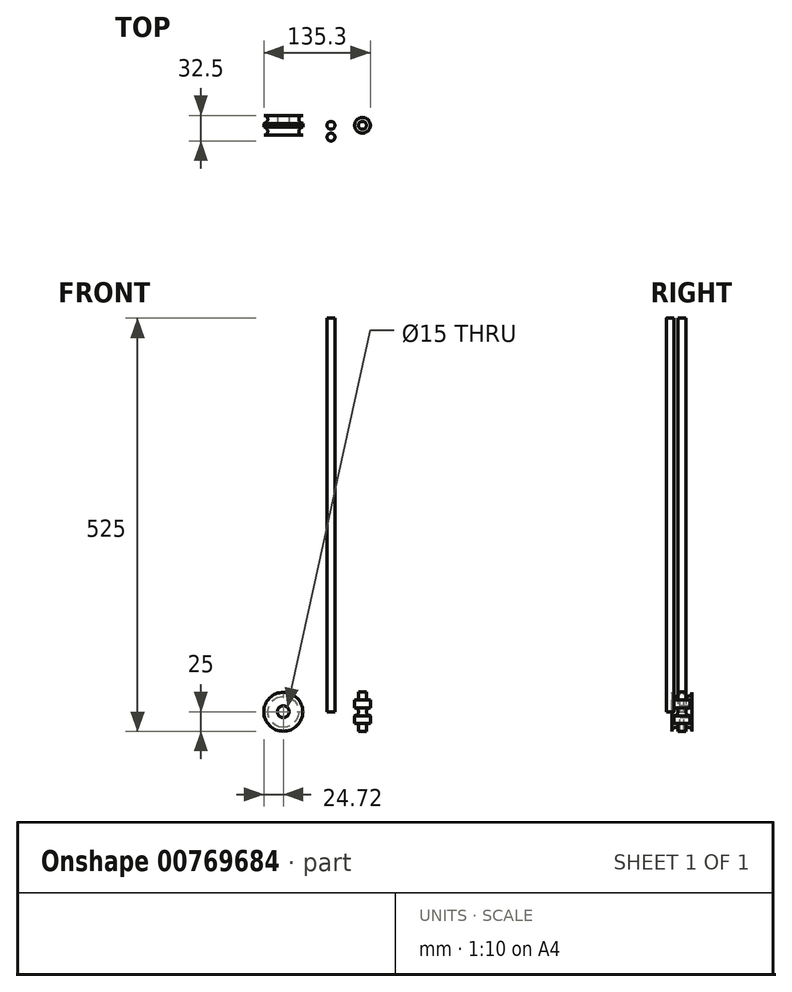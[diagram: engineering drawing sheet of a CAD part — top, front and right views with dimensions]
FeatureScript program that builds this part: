
annotation { "Feature Type Name" : "Feature", "Feature Type Description" : "" }
export const myFeature = defineFeature(function(context is Context, id is Id, definition is map)
    precondition{}
    {
        {
            var Q0;
            Q0=qCreatedBy(makeId("Top.planeOp"),FACE);
            var sketch = newSketch(context, id + "F0", { "sketchPlane" : qUnion([Q0])});
            skCircle(sketch, "E0", {"center": v(0, 0) * mm, "radius": 5 * mm});
            skLineSegment(sketch, "E1", {"start": v(0, 0) * mm, "end": v(0, -15) * mm});
            skCircle(sketch, "E2", {"center": v(0, -15) * mm, "radius": 5 * mm});
            skSolve(sketch);
        }
        {
            var Q0;
            Q0 = qSketchRegion(id + "F0", true);
            extrude(context, id + "F1", {"entities" : qUnion([Q0]), "depth" : 500 * mm, "offsetDistance" : 25 * mm});
        }
        {
            var Q0;
            Q0=qCreatedBy(makeId("Top.planeOp"),FACE);
            var sketch = newSketch(context, id + "F2", { "sketchPlane" : qUnion([Q0])});
            skLineSegment(sketch, "E3", {"start": v(0, 0) * mm, "end": v(40, 0) * mm});
            skCircle(sketch, "E4", {"center": v(40, 0) * mm, "radius": 10 * mm});
            skSolve(sketch);
        }
        {
            var Q0;
            Q0=makeQuery(id+"F2.imprint","IMPRINT",FACE,{"disambiguationData":[TD([[makeQuery(id+"F2.imprint","IMPRINT",EDGE,{"derivedFrom":sQuery(id+"F2.wireOp",EDGE,"E4")}),1.0]])]});
            extrude(context, id + "F3", {"entities" : qUnion([Q0]), "depth" : 50 * mm, "offsetDistance" : 25 * mm, "symmetric" : true});
        }
        {
            var Q0;
            Q0=qCreatedBy(makeId("Right.planeOp"),FACE);
            cPlane(context, id + "F4", {"entities" : qUnion([Q0]), "cplaneType" : CPlaneType.OFFSET, "offset" : 40 * mm, "width" : 150 * mm, "height" : 150 * mm});
        }
        {
            var Q0;
            Q0=qCreatedBy(id+"F4.planeOp",FACE);
            var sketch = newSketch(context, id + "F5", { "sketchPlane" : qUnion([Q0])});
            skLineSegment(sketch, "E5", {"start": v(0, 0) * mm, "end": v(10, 0) * mm});
            skCircle(sketch, "E6", {"center": v(10, 0) * mm, "radius": 5 * mm});
            skLineSegment(sketch, "E7", {"start": v(0, 0) * mm, "end": v(0, 15.21) * mm});
            skSolve(sketch);
        }
        {
            var Q0;
            Q0=makeQuery(id+"F5.imprint","IMPRINT",FACE,{"disambiguationData":[TD([[makeQuery(id+"F5.imprint","IMPRINT",EDGE,{"derivedFrom":sQuery(id+"F5.wireOp",EDGE,"E6")}),1.0]])]});
            var Q1;
            Q1=makeQuery(id+"F3.opExtrude","SWEPT_FACE",FACE,{"disambiguationData":[OSD([sQuery(id+"F2.wireOp",EDGE,"E4")])]});
            revolve(context, id + "F6", {"operationType" : NewBodyOperationType.REMOVE, "surfaceOperationType" : NewSurfaceOperationType.NEW, "entities" : qUnion([Q0]), "axis" : qUnion([Q1]), "revolveType" : RevolveType.FULL, "oppositeDirection" : true});
        }
        {
            var Q0;
            Q0=makeQuery(id+"F3.opExtrude","CAP_FACE",FACE,{"disambiguationData":[OSD([sQuery(id+"F2.wireOp",EDGE,"E4")])],"isStart":false});
            var sketch = newSketch(context, id + "F7", { "sketchPlane" : qUnion([Q0])});
            skCircle(sketch, "E8", {"center": v(40, 0) * mm, "radius": 5 * mm});
            skCircle(sketch, "E9", {"center": v(40, 0) * mm, "radius": 10 * mm});
            skSolve(sketch);
        }
        {
            var Q0;
            Q0 = qSketchRegion(id + "F7", true);
            extrude(context, id + "F8", {"entities" : qUnion([Q0]), "operationType" : NewBodyOperationType.REMOVE, "oppositeDirection" : true, "depth" : 10 * mm, "offsetDistance" : 25 * mm});
        }
        {
            var Q0;
            Q0=makeQuery(id+"F3.opExtrude","CAP_FACE",FACE,{"disambiguationData":[OSD([sQuery(id+"F2.wireOp",EDGE,"E4")])],"isStart":true});
            var sketch = newSketch(context, id + "F9", { "sketchPlane" : qUnion([Q0])});
            skCircle(sketch, "E10", {"center": v(40, 0) * mm, "radius": 5 * mm});
            skCircle(sketch, "E11", {"center": v(40, 0) * mm, "radius": 10 * mm});
            skSolve(sketch);
        }
        {
            var Q0;
            Q0 = qSketchRegion(id + "F9", true);
            extrude(context, id + "F10", {"entities" : qUnion([Q0]), "operationType" : NewBodyOperationType.REMOVE, "oppositeDirection" : true, "depth" : 10 * mm, "offsetDistance" : 25 * mm});
        }
        {
            var Q0;
            Q0=qCreatedBy(makeId("Top.planeOp"),FACE);
            var sketch = newSketch(context, id + "F11", { "sketchPlane" : qUnion([Q0])});
            skLineSegment(sketch, "E12", {"start": v(0, 0) * mm, "end": v(-35.86, 0) * mm});
            skLineSegment(sketch, "E13", {"start": v(-35.86, 0) * mm, "end": v(-35.86, -7.5) * mm});
            skLineSegment(sketch, "E14", {"start": v(-35.86, 0) * mm, "end": v(-35.86, 7.5) * mm});
            skCircle(sketch, "E15", {"center": v(-35.86, 7.5) * mm, "radius": 5 * mm});
            skCircle(sketch, "E16", {"center": v(-35.86, -7.5) * mm, "radius": 5 * mm});
            skLineSegment(sketch, "E17", {"start": v(-35.86, 12.5) * mm, "end": v(-60.58, 12.5) * mm});
            skLineSegment(sketch, "E18", {"start": v(-35.86, -12.5) * mm, "end": v(-60.58, -12.5) * mm});
            skLineSegment(sketch, "E19", {"start": v(-60.58, -12.5) * mm, "end": v(-60.58, 12.5) * mm});
            skLineSegment(sketch, "E20", {"start": v(-35.86, 12.5) * mm, "end": v(-35.86, 7.5) * mm});
            skLineSegment(sketch, "E21", {"start": v(-35.86, -7.5) * mm, "end": v(-35.86, -12.5) * mm});
            skSolve(sketch);
        }
        {
            var Q0;
            {var subQ4=sQuery(id+"F11.wireOp",EDGE,"E17");Q0=makeQuery(id+"F11.imprint","IMPRINT",FACE,{"disambiguationData":[TD([[makeQuery(id+"F11.imprint","IMPRINT",EDGE,{"derivedFrom":subQ4}),1.0]])]});}
            var Q1;
            Q1=sQuery(id+"F11.wireOp",EDGE,"E19");
            revolve(context, id + "F12", {"surfaceOperationType" : NewSurfaceOperationType.NEW, "entities" : qUnion([Q0]), "axis" : qUnion([Q1]), "revolveType" : RevolveType.FULL});
        }
        {
            var Q0;
            Q0=makeQuery(id+"F12.opRevolve","SWEPT_FACE",FACE,{"disambiguationData":[OSD([sQuery(id+"F11.wireOp",EDGE,"E18")])]});
            var sketch = newSketch(context, id + "F13", { "sketchPlane" : qUnion([Q0])});
            skCircle(sketch, "E22", {"center": v(-60.58, 0) * mm, "radius": 7.5 * mm});
            skSolve(sketch);
        }
        {
            var Q0;
            Q0 = qSketchRegion(id + "F13", true);
            extrude(context, id + "F14", {"entities" : qUnion([Q0]), "operationType" : NewBodyOperationType.REMOVE, "oppositeDirection" : true, "depth" : 25 * mm, "offsetDistance" : 25 * mm});
        }
    });
